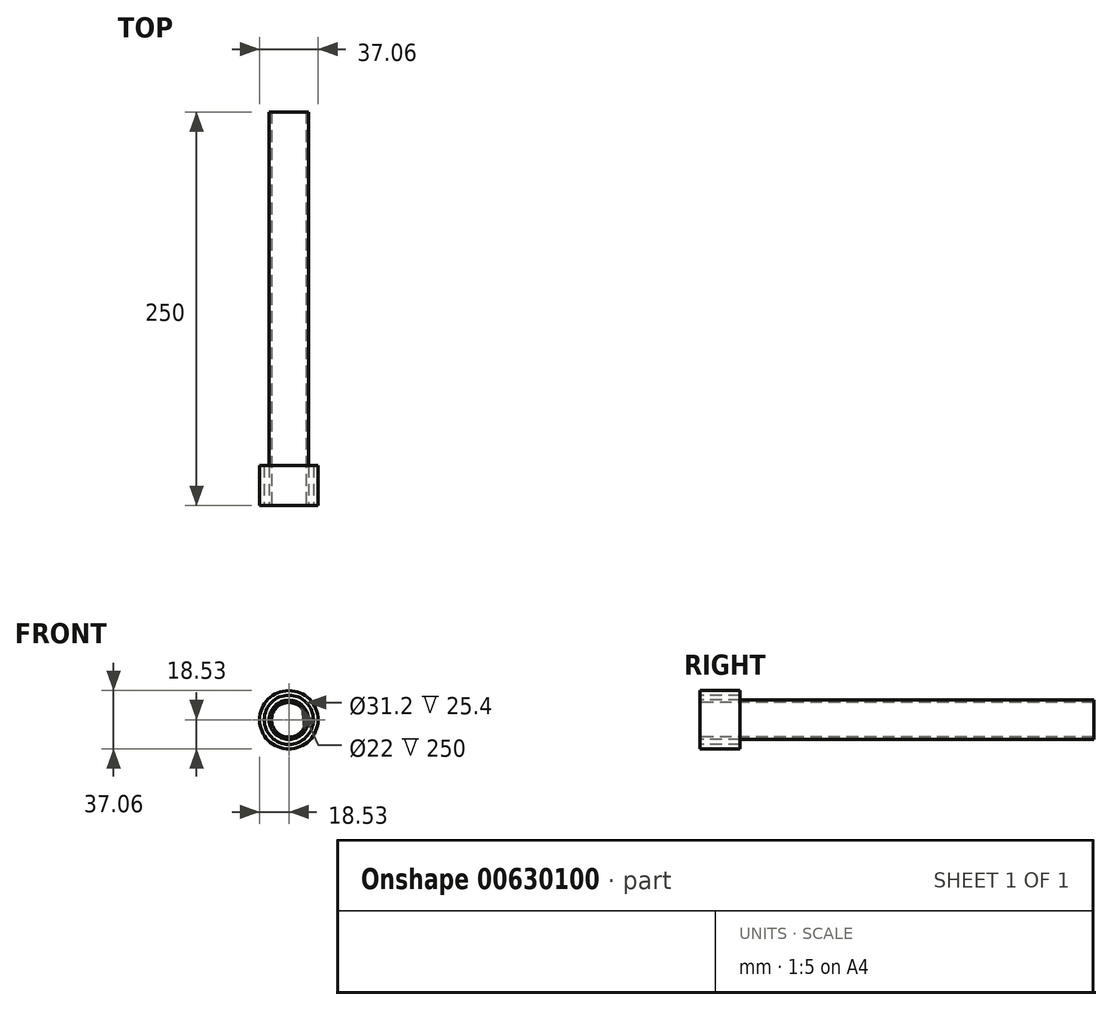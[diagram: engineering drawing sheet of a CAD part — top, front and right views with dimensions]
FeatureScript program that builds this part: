
annotation { "Feature Type Name" : "Feature", "Feature Type Description" : "" }
export const myFeature = defineFeature(function(context is Context, id is Id, definition is map)
    precondition{}
    {
        {
            var Q0;
            Q0=qCreatedBy(makeId("Front.planeOp"),FACE);
            var sketch = newSketch(context, id + "F0", { "sketchPlane" : qUnion([Q0])});
            skCircle(sketch, "E0", {"center": v(0, 0) * mm, "radius": 12.5 * mm});
            skCircle(sketch, "E1", {"center": v(0, 0) * mm, "radius": 11 * mm});
            skSolve(sketch);
        }
        {
            var Q0;
            Q0 = qSketchRegion(id + "F0", true);
            extrude(context, id + "F1", {"entities" : qUnion([Q0]), "oppositeDirection" : true, "depth" : 250 * mm, "offsetDistance" : 25.4 * mm});
        }
        {
            var Q0;
            Q0=qCreatedBy(makeId("Front.planeOp"),FACE);
            var sketch = newSketch(context, id + "F2", { "sketchPlane" : qUnion([Q0])});
            skCircle(sketch, "E2", {"center": v(0, 0) * mm, "radius": 18.53 * mm});
            skCircle(sketch, "E3", {"center": v(0, 0) * mm, "radius": 15.6 * mm});
            skSolve(sketch);
        }
        {
            var Q0;
            Q0 = qSketchRegion(id + "F2", true);
            extrude(context, id + "F3", {"entities" : qUnion([Q0]), "oppositeDirection" : true, "depth" : 25.4 * mm, "offsetDistance" : 25.4 * mm});
        }
    });
